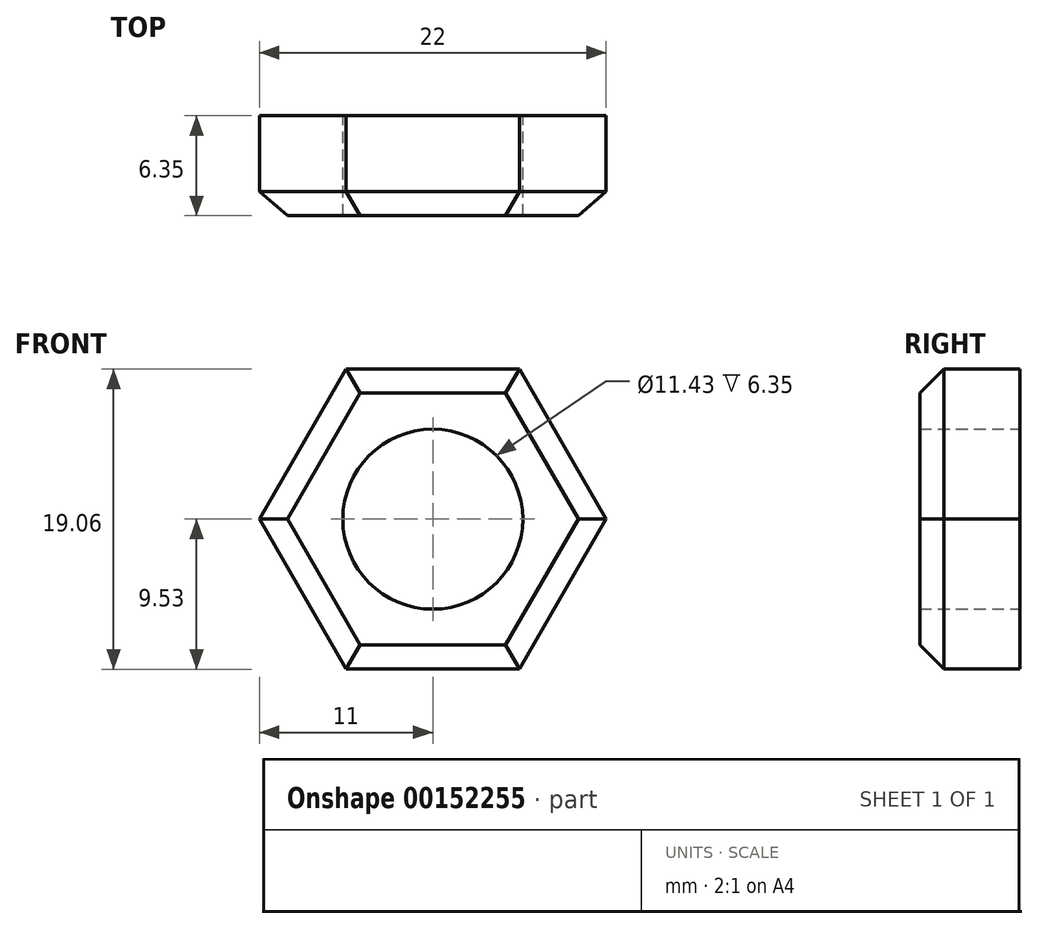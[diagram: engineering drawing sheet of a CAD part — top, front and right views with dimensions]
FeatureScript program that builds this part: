
annotation { "Feature Type Name" : "Feature", "Feature Type Description" : "" }
export const myFeature = defineFeature(function(context is Context, id is Id, definition is map)
    precondition{}
    {
        {
            var Q0;
            Q0=qCreatedBy(makeId("Front.planeOp"),FACE);
            var sketch = newSketch(context, id + "F0", { "sketchPlane" : qUnion([Q0])});
            skCircle(sketch, "E0", {"center": v(0, 0) * mm, "radius": 5.72 * mm});
            skCircle(sketch, "E1.cCircle", {"center": v(0, 0) * mm, "radius": 9.53 * mm, "construction": true});
            skLineSegment(sketch, "E1.0", {"start": v(-5.5, 9.53) * mm, "end": v(5.5, 9.53) * mm});
            skLineSegment(sketch, "E1.1", {"start": v(5.5, 9.53) * mm, "end": v(11, 0) * mm});
            skLineSegment(sketch, "E1.2", {"start": v(11, 0) * mm, "end": v(5.5, -9.53) * mm});
            skLineSegment(sketch, "E1.3", {"start": v(5.5, -9.52) * mm, "end": v(-5.5, -9.53) * mm});
            skLineSegment(sketch, "E1.4", {"start": v(-5.5, -9.53) * mm, "end": v(-11, 0) * mm});
            skLineSegment(sketch, "E1.5", {"start": v(-11, 0) * mm, "end": v(-5.5, 9.53) * mm});
            skPoint(sketch, "E1.0.midPoint", {"position": v(0, 9.53) * mm});
            skSolve(sketch);
        }
        {
            var Q0;
            Q0=makeQuery(id+"F0.imprint","IMPRINT",FACE,{"disambiguationData":[TD([[makeQuery(id+"F0.imprint","IMPRINT",EDGE,{"derivedFrom":sQuery(id+"F0.wireOp",EDGE,"E0")}),-1.0]])]});
            extrude(context, id + "F1", {"entities" : qUnion([Q0]), "depth" : 6.35 * mm});
        }
        {
            var Q0;
            Q0=makeQuery(id+"F1.opExtrude","CAP_EDGE",EDGE,{"disambiguationData":[OSD([sQuery(id+"F0.wireOp",EDGE,"E1.1")])],"isStart":false});
            var Q1;
            Q1=makeQuery(id+"F1.opExtrude","CAP_EDGE",EDGE,{"disambiguationData":[OSD([sQuery(id+"F0.wireOp",EDGE,"E1.0")])],"isStart":false});
            var Q2;
            Q2=makeQuery(id+"F1.opExtrude","CAP_EDGE",EDGE,{"disambiguationData":[OSD([sQuery(id+"F0.wireOp",EDGE,"E1.5")])],"isStart":false});
            var Q3;
            Q3=makeQuery(id+"F1.opExtrude","CAP_EDGE",EDGE,{"disambiguationData":[OSD([sQuery(id+"F0.wireOp",EDGE,"E1.4")])],"isStart":false});
            var Q4;
            Q4=makeQuery(id+"F1.opExtrude","CAP_EDGE",EDGE,{"disambiguationData":[OSD([sQuery(id+"F0.wireOp",EDGE,"E1.3")])],"isStart":false});
            var Q5;
            Q5=makeQuery(id+"F1.opExtrude","CAP_EDGE",EDGE,{"disambiguationData":[OSD([sQuery(id+"F0.wireOp",EDGE,"E1.2")])],"isStart":false});
            chamfer(context, id + "F2", {"entities" : qUnion([Q0, Q1, Q2, Q3, Q4, Q5]), "width" : 1.52 * mm, "tangentPropagation" : true});
        }
    });
